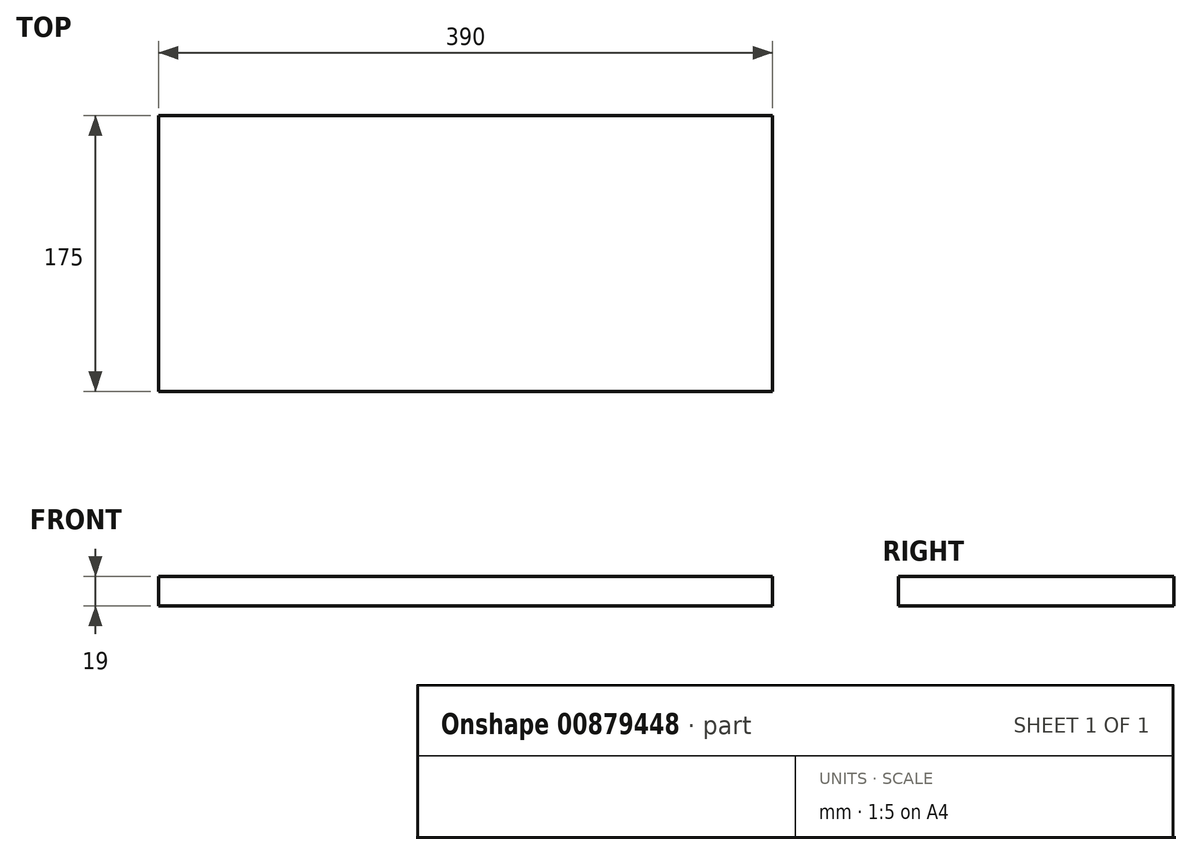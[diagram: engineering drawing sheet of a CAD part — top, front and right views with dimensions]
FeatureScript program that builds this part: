
annotation { "Feature Type Name" : "Feature", "Feature Type Description" : "" }
export const myFeature = defineFeature(function(context is Context, id is Id, definition is map)
    precondition{}
    {
        {
            var Q0;
            Q0=qCreatedBy(makeId("Top.planeOp"),FACE);
            var sketch = newSketch(context, id + "F0", { "sketchPlane" : qUnion([Q0])});
            skLineSegment(sketch, "E0.bottom", {"start": v(-195, 87.5) * mm, "end": v(195, 87.5) * mm});
            skLineSegment(sketch, "E0.top", {"start": v(-195, -87.5) * mm, "end": v(195, -87.5) * mm});
            skLineSegment(sketch, "E0.left", {"start": v(-195, 87.5) * mm, "end": v(-195, -87.5) * mm});
            skLineSegment(sketch, "E0.right", {"start": v(195, 87.5) * mm, "end": v(195, -87.5) * mm});
            skPoint(sketch, "E0.middle", {"position": v(0, 0) * mm});
            skSolve(sketch);
        }
        {
            var Q0;
            Q0=makeQuery(id+"F0.imprint","IMPRINT",FACE,{"disambiguationData":[TD([[makeQuery(id+"F0.imprint","IMPRINT",EDGE,{"derivedFrom":sQuery(id+"F0.wireOp",EDGE,"E0.bottom")}),-1.0]])]});
            extrude(context, id + "F1", {"entities" : qUnion([Q0]), "flatOperationType" : FlatOperationType.REMOVE, "depth" : 19 * mm, "offsetDistance" : 25 * mm, "domain" : OperationDomain.MODEL});
        }
    });
